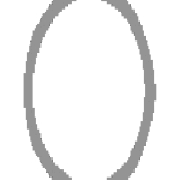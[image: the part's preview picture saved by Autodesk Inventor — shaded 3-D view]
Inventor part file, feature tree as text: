
AUTODESK INVENTOR PART (.ipt)
format: ipt  version: 2021 (Build 250183000, 183)  size: 115,712 bytes
history: native  units: in
note: dims shown in document units (in); Inventor stores cm internally (conversion verified against a paired STEP export)
features: other x4, sketch x3, plane x1
ambient origin geometry x8: Origin, YZ Plane, XZ Plane, XY Plane, X Axis, Y Axis, Z Axis, Center Point
bodies: Solid1 (feature_tree), Body (feature_tree)
feature tree (8):
  other  "Driven Length"
  other  "Frame Generator"
  other  "Start Plane"
  other  "End Plane"
  sketch  "Sketch"  dims[d2=1.3416in d4=-0.0in d5=1.3416in d6=0.12in d7=0.0in d8=90.0deg d9=1.3416in]
  sketch  "Sketch2"  dims[d0=1.0in]
  plane  "Work Plane3"
  sketch  "Sketch3"  dims[d1=0.065in]
